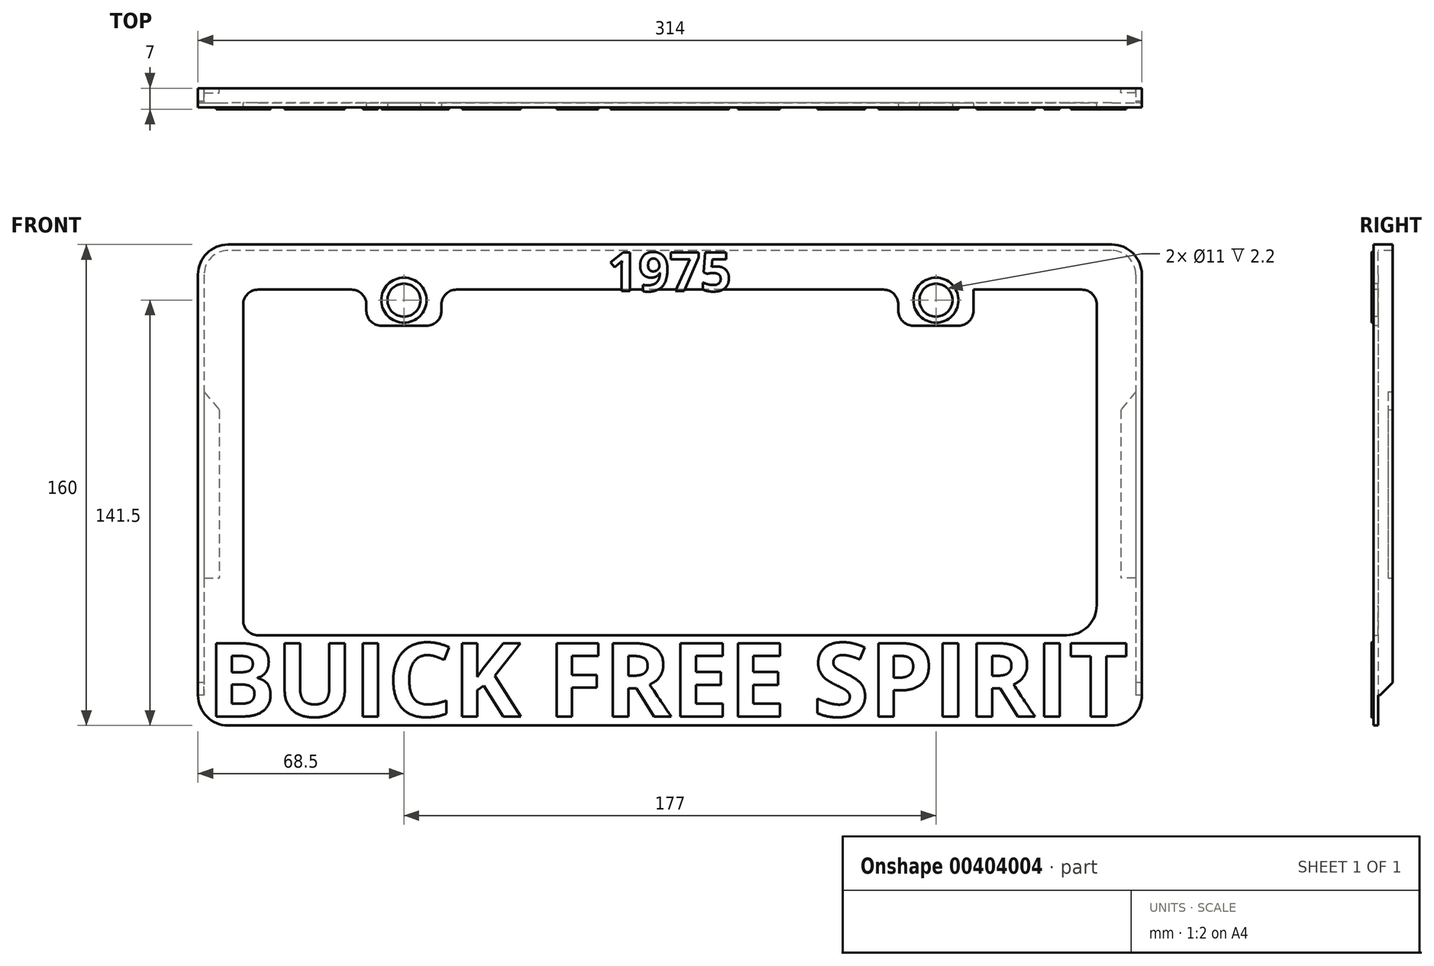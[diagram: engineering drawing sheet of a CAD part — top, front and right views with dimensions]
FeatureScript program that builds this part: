
annotation { "Feature Type Name" : "Feature", "Feature Type Description" : "" }
export const myFeature = defineFeature(function(context is Context, id is Id, definition is map)
    precondition{}
    {
        {
            var Q0;
            Q0=qCreatedBy(makeId("Front.planeOp"),FACE);
            var sketch = newSketch(context, id + "F0", { "sketchPlane" : qUnion([Q0])});
            skLineSegment(sketch, "E0.bottom", {"start": v(147, 80) * mm, "end": v(-147, 80) * mm});
            skLineSegment(sketch, "E0.top", {"start": v(147, -80) * mm, "end": v(-147, -80) * mm});
            skLineSegment(sketch, "E0.left", {"start": v(157, 70) * mm, "end": v(157, -70) * mm});
            skLineSegment(sketch, "E0.right", {"start": v(-157, 70) * mm, "end": v(-157, -70) * mm});
            skPoint(sketch, "E0.middle", {"position": v(0, 0) * mm});
            skLineSegment(sketch, "E1.bottom", {"start": v(137, 65) * mm, "end": v(-137, 65) * mm});
            skLineSegment(sketch, "E1.left", {"start": v(142, 60) * mm, "end": v(142, -40) * mm});
            skLineSegment(sketch, "E1.right", {"start": v(-142, 60) * mm, "end": v(-142, -45) * mm});
            skLineSegment(sketch, "E2", {"start": v(-137, -50) * mm, "end": v(132, -50) * mm});
            skPoint(sketch, "E3.orphan", {"position": v(142, -65) * mm});
            skPoint(sketch, "E4.orphan", {"position": v(-142, -65) * mm});
            skPoint(sketch, "E5.visualSharp", {"position": v(-157, 80) * mm});
            skArc(sketch, "E5.filletArc", {"start": v(-147, 80) * mm, "mid": v(-154.07, 77.07) * mm, "end": v(-157, 70) * mm});
            skPoint(sketch, "E6.visualSharp", {"position": v(-157, -80) * mm});
            skArc(sketch, "E6.filletArc", {"start": v(-157, -70) * mm, "mid": v(-154.07, -77.07) * mm, "end": v(-147, -80) * mm});
            skPoint(sketch, "E7.visualSharp", {"position": v(157, 80) * mm});
            skArc(sketch, "E7.filletArc", {"start": v(157, 70) * mm, "mid": v(154.07, 77.07) * mm, "end": v(147, 80) * mm});
            skPoint(sketch, "E8.visualSharp", {"position": v(157, -80) * mm});
            skArc(sketch, "E8.filletArc", {"start": v(147, -80) * mm, "mid": v(154.07, -77.07) * mm, "end": v(157, -70) * mm});
            skPoint(sketch, "E9.visualSharp", {"position": v(-142, 65) * mm});
            skArc(sketch, "E9.filletArc", {"start": v(-137, 65) * mm, "mid": v(-140.54, 63.54) * mm, "end": v(-142, 60) * mm});
            skPoint(sketch, "E10.visualSharp", {"position": v(-142, -50) * mm});
            skArc(sketch, "E10.filletArc", {"start": v(-142, -45) * mm, "mid": v(-140.54, -48.54) * mm, "end": v(-137, -50) * mm});
            skPoint(sketch, "E11.visualSharp", {"position": v(142, -50) * mm});
            skArc(sketch, "E11.filletArc", {"start": v(132, -50) * mm, "mid": v(139.07, -47.07) * mm, "end": v(142, -40) * mm});
            skPoint(sketch, "E12.visualSharp", {"position": v(142, 65) * mm});
            skArc(sketch, "E12.filletArc", {"start": v(142, 60) * mm, "mid": v(140.54, 63.54) * mm, "end": v(137, 65) * mm});
            skSolve(sketch);
        }
        {
            var Q0;
            Q0=qSketchRegion(id+"F0",true);
            extrude(context, id + "F1", {"entities" : qUnion([Q0]), "depth" : 1.6 * mm, "offsetDistance" : 25 * mm});
        }
        {
            var Q0;
            Q0=makeQuery(id+"F1.opExtrude","CAP_FACE",FACE,{"disambiguationData":[OSD([sQuery(id+"F0.wireOp",EDGE,"E0.bottom"),sQuery(id+"F0.wireOp",EDGE,"E0.top"),sQuery(id+"F0.wireOp",EDGE,"E0.left"),sQuery(id+"F0.wireOp",EDGE,"E0.right"),sQuery(id+"F0.wireOp",EDGE,"E1.bottom"),sQuery(id+"F0.wireOp",EDGE,"E1.left"),sQuery(id+"F0.wireOp",EDGE,"E1.right"),sQuery(id+"F0.wireOp",EDGE,"E2"),sQuery(id+"F0.wireOp",EDGE,"E5.filletArc"),sQuery(id+"F0.wireOp",EDGE,"E6.filletArc"),sQuery(id+"F0.wireOp",EDGE,"E7.filletArc"),sQuery(id+"F0.wireOp",EDGE,"E8.filletArc"),sQuery(id+"F0.wireOp",EDGE,"E9.filletArc"),sQuery(id+"F0.wireOp",EDGE,"E10.filletArc"),sQuery(id+"F0.wireOp",EDGE,"E11.filletArc"),sQuery(id+"F0.wireOp",EDGE,"E12.filletArc")])],"isStart":false});
            var sketch = newSketch(context, id + "F2", { "sketchPlane" : qUnion([Q0])});
            skLineSegment(sketch, "E13.bottom", {"start": v(-101, 65) * mm, "end": v(-76, 65) * mm});
            skLineSegment(sketch, "E13.top", {"start": v(-101, 53) * mm, "end": v(-76, 53) * mm});
            skLineSegment(sketch, "E13.left", {"start": v(-101, 65) * mm, "end": v(-101, 53) * mm});
            skLineSegment(sketch, "E13.right", {"start": v(-76, 65) * mm, "end": v(-76, 53) * mm});
            skLineSegment(sketch, "E14.bottom", {"start": v(76, 65) * mm, "end": v(101, 65) * mm});
            skLineSegment(sketch, "E14.top", {"start": v(76, 53) * mm, "end": v(101, 53) * mm});
            skLineSegment(sketch, "E14.left", {"start": v(76, 65) * mm, "end": v(76, 53) * mm});
            skLineSegment(sketch, "E14.right", {"start": v(101, 65) * mm, "end": v(101, 53) * mm});
            skLineSegment(sketch, "E15", {"start": v(-88.5, 53) * mm, "end": v(-88.5, 65) * mm, "construction": true});
            skLineSegment(sketch, "E16", {"start": v(-101, 53) * mm, "end": v(-142, 53) * mm, "construction": true});
            skLineSegment(sketch, "E17", {"start": v(101, 53) * mm, "end": v(142, 53) * mm, "construction": true});
            skSolve(sketch);
        }
        {
            var Q0;
            Q0=qSketchRegion(id+"F2",true);
            var Q1;
            Q1=makeQuery(id+"F1.opExtrude","CAP_FACE",FACE,{"disambiguationData":[OSD([sQuery(id+"F0.wireOp",EDGE,"E0.bottom"),sQuery(id+"F0.wireOp",EDGE,"E0.top"),sQuery(id+"F0.wireOp",EDGE,"E0.left"),sQuery(id+"F0.wireOp",EDGE,"E0.right"),sQuery(id+"F0.wireOp",EDGE,"E1.bottom"),sQuery(id+"F0.wireOp",EDGE,"E1.left"),sQuery(id+"F0.wireOp",EDGE,"E1.right"),sQuery(id+"F0.wireOp",EDGE,"E2"),sQuery(id+"F0.wireOp",EDGE,"E5.filletArc"),sQuery(id+"F0.wireOp",EDGE,"E6.filletArc"),sQuery(id+"F0.wireOp",EDGE,"E7.filletArc"),sQuery(id+"F0.wireOp",EDGE,"E8.filletArc"),sQuery(id+"F0.wireOp",EDGE,"E9.filletArc"),sQuery(id+"F0.wireOp",EDGE,"E10.filletArc"),sQuery(id+"F0.wireOp",EDGE,"E11.filletArc"),sQuery(id+"F0.wireOp",EDGE,"E12.filletArc")])],"isStart":true});
            extrude(context, id + "F3", {"entities" : qUnion([Q0]), "operationType" : NewBodyOperationType.ADD, "endBound" : BoundingType.UP_TO_SURFACE, "oppositeDirection" : true, "endBoundEntityFace" : qUnion([Q1]), "depth" : 25 * mm});
        }
        {
            var Q0;
            Q0=makeQuery(id+"F3.boolean.opBoolean","MERGE",FACE,{"derivedFrom":[makeQuery(id+"F1.opExtrude","CAP_FACE",FACE,{"disambiguationData":[OSD([sQuery(id+"F0.wireOp",EDGE,"E0.bottom"),sQuery(id+"F0.wireOp",EDGE,"E0.top"),sQuery(id+"F0.wireOp",EDGE,"E0.left"),sQuery(id+"F0.wireOp",EDGE,"E0.right"),sQuery(id+"F0.wireOp",EDGE,"E1.bottom"),sQuery(id+"F0.wireOp",EDGE,"E1.left"),sQuery(id+"F0.wireOp",EDGE,"E1.right"),sQuery(id+"F0.wireOp",EDGE,"E2"),sQuery(id+"F0.wireOp",EDGE,"E5.filletArc"),sQuery(id+"F0.wireOp",EDGE,"E6.filletArc"),sQuery(id+"F0.wireOp",EDGE,"E7.filletArc"),sQuery(id+"F0.wireOp",EDGE,"E8.filletArc"),sQuery(id+"F0.wireOp",EDGE,"E9.filletArc"),sQuery(id+"F0.wireOp",EDGE,"E10.filletArc"),sQuery(id+"F0.wireOp",EDGE,"E11.filletArc"),sQuery(id+"F0.wireOp",EDGE,"E12.filletArc")])],"isStart":false}),makeQuery(id+"F3.opExtrude","CAP_FACE",FACE,{"disambiguationData":[OSD([sQuery(id+"F2.wireOp",EDGE,"E13.bottom"),sQuery(id+"F2.wireOp",EDGE,"E13.top"),sQuery(id+"F2.wireOp",EDGE,"E13.left"),sQuery(id+"F2.wireOp",EDGE,"E13.right")])],"isStart":true}),makeQuery(id+"F3.opExtrude","CAP_FACE",FACE,{"disambiguationData":[OSD([sQuery(id+"F2.wireOp",EDGE,"E14.bottom"),sQuery(id+"F2.wireOp",EDGE,"E14.top"),sQuery(id+"F2.wireOp",EDGE,"E14.left"),sQuery(id+"F2.wireOp",EDGE,"E14.right")])],"isStart":true})]});
            var sketch = newSketch(context, id + "F4", { "sketchPlane" : qUnion([Q0])});
            skLineSegment(sketch, "E18", {"start": v(101, 55) * mm, "end": v(101, 65) * mm});
            skLineSegment(sketch, "E19", {"start": v(101, 55) * mm, "end": v(142, 55) * mm});
            skLineSegment(sketch, "E20", {"start": v(142, 60) * mm, "end": v(101, 60) * mm});
            skLineSegment(sketch, "E21", {"start": v(142, 55) * mm, "end": v(142, 60) * mm});
            skLineSegment(sketch, "E22", {"start": v(101, 65) * mm, "end": v(101, 60) * mm});
            skSolve(sketch);
        }
        {
            var Q0;
            Q0=makeQuery(id+"F3.opExtrude","SWEPT_EDGE",EDGE,{"disambiguationData":[OSD([sQuery(id+"F2.wireOp",EDGE,"E13.top"),sQuery(id+"F2.wireOp",EDGE,"E13.left")])]});
            var Q1;
            Q1=makeQuery(id+"F3.opExtrude","SWEPT_EDGE",EDGE,{"disambiguationData":[OSD([sQuery(id+"F0.wireOp",EDGE,"E1.bottom"),sQuery(id+"F2.wireOp",EDGE,"E13.bottom"),sQuery(id+"F2.wireOp",EDGE,"E13.left")])]});
            var Q2;
            Q2=makeQuery(id+"F3.opExtrude","SWEPT_EDGE",EDGE,{"disambiguationData":[OSD([sQuery(id+"F2.wireOp",EDGE,"E13.top"),sQuery(id+"F2.wireOp",EDGE,"E13.right")])]});
            var Q3;
            Q3=makeQuery(id+"F3.opExtrude","SWEPT_EDGE",EDGE,{"disambiguationData":[OSD([sQuery(id+"F0.wireOp",EDGE,"E1.bottom"),sQuery(id+"F2.wireOp",EDGE,"E13.bottom"),sQuery(id+"F2.wireOp",EDGE,"E13.right")])]});
            var Q4;
            Q4=makeQuery(id+"F3.opExtrude","SWEPT_EDGE",EDGE,{"disambiguationData":[OSD([sQuery(id+"F2.wireOp",EDGE,"E14.top"),sQuery(id+"F2.wireOp",EDGE,"E14.right")])]});
            var Q5;
            Q5=makeQuery(id+"F3.opExtrude","SWEPT_EDGE",EDGE,{"disambiguationData":[OSD([sQuery(id+"F0.wireOp",EDGE,"E1.bottom"),sQuery(id+"F2.wireOp",EDGE,"E14.bottom"),sQuery(id+"F2.wireOp",EDGE,"E14.right")])]});
            var Q6;
            Q6=makeQuery(id+"F3.opExtrude","SWEPT_EDGE",EDGE,{"disambiguationData":[OSD([sQuery(id+"F2.wireOp",EDGE,"E14.top"),sQuery(id+"F2.wireOp",EDGE,"E14.left")])]});
            var Q7;
            Q7=makeQuery(id+"F3.opExtrude","SWEPT_EDGE",EDGE,{"disambiguationData":[OSD([sQuery(id+"F0.wireOp",EDGE,"E1.bottom"),sQuery(id+"F2.wireOp",EDGE,"E14.bottom"),sQuery(id+"F2.wireOp",EDGE,"E14.left")])]});
            var Q8;
            Q8=makeQuery(id+"FJHd9evdb0oNIyS_1.boolean.opBoolean","COPY",EDGE,{"derivedFrom":makeQuery(id+"FJHd9evdb0oNIyS_1.opExtrude","SWEPT_EDGE",EDGE,{"disambiguationData":[OSD([sQuery(id+"F4.wireOp",EDGE,"E19"),sQuery(id+"F4.wireOp",EDGE,"E21")])]})});
            fillet(context, id + "F5", {"entities" : qUnion([Q0, Q1, Q2, Q3, Q4, Q5, Q6, Q7, Q8]), "radius" : 5 * mm, "tangentPropagation" : true, "allowEdgeOverflow" : false});
        }
        {
            var Q0;
            Q0=makeQuery(id+"F3.boolean.opBoolean","MERGE",FACE,{"derivedFrom":[makeQuery(id+"F1.opExtrude","CAP_FACE",FACE,{"disambiguationData":[OSD([sQuery(id+"F0.wireOp",EDGE,"E0.bottom"),sQuery(id+"F0.wireOp",EDGE,"E0.top"),sQuery(id+"F0.wireOp",EDGE,"E0.left"),sQuery(id+"F0.wireOp",EDGE,"E0.right"),sQuery(id+"F0.wireOp",EDGE,"E1.bottom"),sQuery(id+"F0.wireOp",EDGE,"E1.left"),sQuery(id+"F0.wireOp",EDGE,"E1.right"),sQuery(id+"F0.wireOp",EDGE,"E2"),sQuery(id+"F0.wireOp",EDGE,"E5.filletArc"),sQuery(id+"F0.wireOp",EDGE,"E6.filletArc"),sQuery(id+"F0.wireOp",EDGE,"E7.filletArc"),sQuery(id+"F0.wireOp",EDGE,"E8.filletArc"),sQuery(id+"F0.wireOp",EDGE,"E9.filletArc"),sQuery(id+"F0.wireOp",EDGE,"E10.filletArc"),sQuery(id+"F0.wireOp",EDGE,"E11.filletArc"),sQuery(id+"F0.wireOp",EDGE,"E12.filletArc")])],"isStart":false}),makeQuery(id+"F3.opExtrude","CAP_FACE",FACE,{"disambiguationData":[OSD([sQuery(id+"F2.wireOp",EDGE,"E13.bottom"),sQuery(id+"F2.wireOp",EDGE,"E13.top"),sQuery(id+"F2.wireOp",EDGE,"E13.left"),sQuery(id+"F2.wireOp",EDGE,"E13.right")])],"isStart":true}),makeQuery(id+"F3.opExtrude","CAP_FACE",FACE,{"disambiguationData":[OSD([sQuery(id+"F2.wireOp",EDGE,"E14.bottom"),sQuery(id+"F2.wireOp",EDGE,"E14.top"),sQuery(id+"F2.wireOp",EDGE,"E14.left"),sQuery(id+"F2.wireOp",EDGE,"E14.right")])],"isStart":true})]});
            var sketch = newSketch(context, id + "F6", { "sketchPlane" : qUnion([Q0])});
            skCircle(sketch, "E23", {"center": v(-88.5, 61.5) * mm, "radius": 5.5 * mm});
            skCircle(sketch, "E24", {"center": v(88.5, 61.5) * mm, "radius": 5.5 * mm});
            skLineSegment(sketch, "E25", {"start": v(-88.5, 49) * mm, "end": v(-88.5, 94.48) * mm, "construction": true});
            skLineSegment(sketch, "E26", {"start": v(88.5, 49) * mm, "end": v(88.5, 72.42) * mm, "construction": true});
            skSolve(sketch);
        }
        {
            var Q0;
            Q0=qSketchRegion(id+"F6",true);
            extrude(context, id + "F7", {"entities" : qUnion([Q0]), "operationType" : NewBodyOperationType.REMOVE, "oppositeDirection" : true, "depth" : 25 * mm});
        }
        {
            var Q0;
            Q0=makeQuery(id+"F3.boolean.opBoolean","MERGE",FACE,{"derivedFrom":[makeQuery(id+"F1.opExtrude","CAP_FACE",FACE,{"disambiguationData":[OSD([sQuery(id+"F0.wireOp",EDGE,"E0.bottom"),sQuery(id+"F0.wireOp",EDGE,"E0.top"),sQuery(id+"F0.wireOp",EDGE,"E0.left"),sQuery(id+"F0.wireOp",EDGE,"E0.right"),sQuery(id+"F0.wireOp",EDGE,"E1.bottom"),sQuery(id+"F0.wireOp",EDGE,"E1.left"),sQuery(id+"F0.wireOp",EDGE,"E1.right"),sQuery(id+"F0.wireOp",EDGE,"E2"),sQuery(id+"F0.wireOp",EDGE,"E5.filletArc"),sQuery(id+"F0.wireOp",EDGE,"E6.filletArc"),sQuery(id+"F0.wireOp",EDGE,"E7.filletArc"),sQuery(id+"F0.wireOp",EDGE,"E8.filletArc"),sQuery(id+"F0.wireOp",EDGE,"E9.filletArc"),sQuery(id+"F0.wireOp",EDGE,"E10.filletArc"),sQuery(id+"F0.wireOp",EDGE,"E11.filletArc"),sQuery(id+"F0.wireOp",EDGE,"E12.filletArc")])],"isStart":false}),makeQuery(id+"F3.opExtrude","CAP_FACE",FACE,{"disambiguationData":[OSD([sQuery(id+"F2.wireOp",EDGE,"E13.bottom"),sQuery(id+"F2.wireOp",EDGE,"E13.top"),sQuery(id+"F2.wireOp",EDGE,"E13.left"),sQuery(id+"F2.wireOp",EDGE,"E13.right")])],"isStart":true}),makeQuery(id+"F3.opExtrude","CAP_FACE",FACE,{"disambiguationData":[OSD([sQuery(id+"F2.wireOp",EDGE,"E14.bottom"),sQuery(id+"F2.wireOp",EDGE,"E14.top"),sQuery(id+"F2.wireOp",EDGE,"E14.left"),sQuery(id+"F2.wireOp",EDGE,"E14.right")])],"isStart":true})]});
            var sketch = newSketch(context, id + "F8", { "sketchPlane" : qUnion([Q0])});
            skText(sketch, "E27", { "text": "1975", "fontName": "OpenSans-Bold.ttf"});
            const initialGuessF8  = {"E27": [-0.0208, 0.0645, 1, 0, 0.013]};
            skSetInitialGuess(sketch, initialGuessF8);
            skSolve(sketch);
        }
        {
            var Q0;
            Q0=qSketchRegion(id+"F8",true);
            extrude(context, id + "F9", {"entities" : qUnion([Q0]), "operationType" : NewBodyOperationType.ADD, "offsetDistance" : 25 * mm, "depth" : .6 * mm});
        }
        {
            var Q0;
            {var subQ0=sQuery(id+"F0.wireOp",EDGE,"E0.right");var subQ2=sQuery(id+"F2.wireOp",EDGE,"E14.left");var subQ3=sQuery(id+"F2.wireOp",EDGE,"E14.bottom");var subQ4=sQuery(id+"F0.wireOp",EDGE,"E1.bottom");var subQ5=sQuery(id+"F2.wireOp",EDGE,"E14.right");var subQ6=sQuery(id+"F2.wireOp",EDGE,"E14.top");var subQ7=sQuery(id+"F0.wireOp",EDGE,"E8.filletArc");var subQ8=sQuery(id+"F0.wireOp",EDGE,"E5.filletArc");var subQ9=sQuery(id+"F0.wireOp",EDGE,"E7.filletArc");var subQ10=sQuery(id+"F0.wireOp",EDGE,"E2");var subQ11=sQuery(id+"F0.wireOp",EDGE,"E6.filletArc");var subQ12=sQuery(id+"F0.wireOp",EDGE,"E1.right");var subQ13=sQuery(id+"F2.wireOp",EDGE,"E13.right");var subQ14=sQuery(id+"F2.wireOp",EDGE,"E13.top");var subQ15=sQuery(id+"F0.wireOp",EDGE,"E1.left");var subQ16=sQuery(id+"F0.wireOp",EDGE,"E9.filletArc");var subQ17=sQuery(id+"F2.wireOp",EDGE,"E13.bottom");var subQ18=sQuery(id+"F0.wireOp",EDGE,"E0.bottom");var subQ19=sQuery(id+"F0.wireOp",EDGE,"E0.top");var subQ20=sQuery(id+"F0.wireOp",EDGE,"E0.left");var subQ21=sQuery(id+"F0.wireOp",EDGE,"E10.filletArc");var subQ23=sQuery(id+"F2.wireOp",EDGE,"E13.left");var subQ24=sQuery(id+"F0.wireOp",EDGE,"E11.filletArc");Q0=makeQuery(id+"F9.boolean.opBoolean","SPLIT",FACE,{"disambiguationData":[TD([makeQuery(id+"F1.opExtrude","SWEPT_FACE",FACE,{"disambiguationData":[OSD([subQ18])]})])],"derivedFrom":makeQuery(id+"F3.boolean.opBoolean","MERGE",FACE,{"derivedFrom":[makeQuery(id+"F1.opExtrude","CAP_FACE",FACE,{"disambiguationData":[OSD([subQ18,subQ19,subQ20,subQ0,subQ4,subQ15,subQ12,subQ10,subQ8,subQ11,subQ9,subQ7,subQ16,subQ21,subQ24,sQuery(id+"F0.wireOp",EDGE,"E12.filletArc")])],"isStart":false}),makeQuery(id+"F3.opExtrude","CAP_FACE",FACE,{"disambiguationData":[OSD([subQ17,subQ14,subQ23,subQ13])],"isStart":true}),makeQuery(id+"F3.opExtrude","CAP_FACE",FACE,{"disambiguationData":[OSD([subQ3,subQ6,subQ2,subQ5])],"isStart":true})]})});}
            var sketch = newSketch(context, id + "F10", { "sketchPlane" : qUnion([Q0])});
            skText(sketch, "E28", { "text": "75", "fontName": "OpenSans-Bold.ttf"});
            const initialGuessF10  = {"E28": [0.11823, -0.0765, 1, 0, 0.02]};
            skSetInitialGuess(sketch, initialGuessF10);
            skSolve(sketch);
        }
        {
            var Q0;
            {var subQ0=sQuery(id+"F0.wireOp",EDGE,"E0.right");var subQ2=sQuery(id+"F2.wireOp",EDGE,"E14.left");var subQ3=sQuery(id+"F2.wireOp",EDGE,"E14.bottom");var subQ4=sQuery(id+"F0.wireOp",EDGE,"E1.bottom");var subQ5=sQuery(id+"F2.wireOp",EDGE,"E14.right");var subQ6=sQuery(id+"F2.wireOp",EDGE,"E14.top");var subQ7=sQuery(id+"F0.wireOp",EDGE,"E8.filletArc");var subQ8=sQuery(id+"F0.wireOp",EDGE,"E5.filletArc");var subQ9=sQuery(id+"F0.wireOp",EDGE,"E7.filletArc");var subQ10=sQuery(id+"F0.wireOp",EDGE,"E2");var subQ11=sQuery(id+"F0.wireOp",EDGE,"E6.filletArc");var subQ12=sQuery(id+"F0.wireOp",EDGE,"E1.right");var subQ13=sQuery(id+"F2.wireOp",EDGE,"E13.right");var subQ14=sQuery(id+"F2.wireOp",EDGE,"E13.top");var subQ15=sQuery(id+"F0.wireOp",EDGE,"E1.left");var subQ16=sQuery(id+"F0.wireOp",EDGE,"E9.filletArc");var subQ17=sQuery(id+"F2.wireOp",EDGE,"E13.bottom");var subQ18=sQuery(id+"F0.wireOp",EDGE,"E0.bottom");var subQ19=sQuery(id+"F0.wireOp",EDGE,"E0.top");var subQ20=sQuery(id+"F0.wireOp",EDGE,"E0.left");var subQ21=sQuery(id+"F0.wireOp",EDGE,"E10.filletArc");var subQ23=sQuery(id+"F2.wireOp",EDGE,"E13.left");var subQ24=sQuery(id+"F0.wireOp",EDGE,"E11.filletArc");Q0=makeQuery(id+"F9.boolean.opBoolean","SPLIT",FACE,{"disambiguationData":[TD([makeQuery(id+"F1.opExtrude","SWEPT_FACE",FACE,{"disambiguationData":[OSD([subQ18])]})])],"derivedFrom":makeQuery(id+"F3.boolean.opBoolean","MERGE",FACE,{"derivedFrom":[makeQuery(id+"F1.opExtrude","CAP_FACE",FACE,{"disambiguationData":[OSD([subQ18,subQ19,subQ20,subQ0,subQ4,subQ15,subQ12,subQ10,subQ8,subQ11,subQ9,subQ7,subQ16,subQ21,subQ24,sQuery(id+"F0.wireOp",EDGE,"E12.filletArc")])],"isStart":false}),makeQuery(id+"F3.opExtrude","CAP_FACE",FACE,{"disambiguationData":[OSD([subQ17,subQ14,subQ23,subQ13])],"isStart":true}),makeQuery(id+"F3.opExtrude","CAP_FACE",FACE,{"disambiguationData":[OSD([subQ3,subQ6,subQ2,subQ5])],"isStart":true})]})});}
            var sketch = newSketch(context, id + "F11", { "sketchPlane" : qUnion([Q0])});
            skText(sketch, "E29", { "text": "BUICK FREE SPIRIT", "fontName": "OpenSans-Bold.ttf"});
            const initialGuessF11  = {"E29": [-0.154, -0.077, 1, 0, 0.02455]};
            skSetInitialGuess(sketch, initialGuessF11);
            skSolve(sketch);
        }
        {
            var Q0;
            Q0=qSketchRegion(id+"F11",true);
            extrude(context, id + "F12", {"entities" : qUnion([Q0]), "operationType" : NewBodyOperationType.ADD, "offsetDistance" : 25 * mm, "depth" : .6 * mm});
        }
        {
            var Q0;
            {var subQ0=sQuery(id+"F0.wireOp",EDGE,"E12.filletArc");var subQ1=sQuery(id+"F0.wireOp",EDGE,"E11.filletArc");var subQ2=sQuery(id+"F0.wireOp",EDGE,"E10.filletArc");var subQ3=sQuery(id+"F0.wireOp",EDGE,"E9.filletArc");var subQ4=sQuery(id+"F0.wireOp",EDGE,"E8.filletArc");var subQ5=sQuery(id+"F0.wireOp",EDGE,"E7.filletArc");var subQ6=sQuery(id+"F0.wireOp",EDGE,"E6.filletArc");var subQ7=sQuery(id+"F0.wireOp",EDGE,"E5.filletArc");var subQ8=sQuery(id+"F0.wireOp",EDGE,"E2");var subQ9=sQuery(id+"F0.wireOp",EDGE,"E1.right");var subQ10=sQuery(id+"F0.wireOp",EDGE,"E1.left");var subQ11=sQuery(id+"F0.wireOp",EDGE,"E1.bottom");var subQ12=sQuery(id+"F0.wireOp",EDGE,"E0.right");var subQ13=sQuery(id+"F0.wireOp",EDGE,"E0.left");var subQ14=sQuery(id+"F0.wireOp",EDGE,"E0.top");var subQ15=sQuery(id+"F0.wireOp",EDGE,"E0.bottom");Q0=makeQuery(id+"F3.boolean.opBoolean","MERGE",FACE,{"derivedFrom":[makeQuery(id+"F1.opExtrude","CAP_FACE",FACE,{"disambiguationData":[OSD([subQ15,subQ14,subQ13,subQ12,subQ11,subQ10,subQ9,subQ8,subQ7,subQ6,subQ5,subQ4,subQ3,subQ2,subQ1,subQ0])],"isStart":true}),makeQuery(id+"F3.opExtrude","CAP_FACE",FACE,{"disambiguationData":[OSD([subQ15,subQ14,subQ13,subQ12,subQ11,subQ10,subQ9,subQ8,subQ7,subQ6,subQ5,subQ4,subQ3,subQ2,subQ1,subQ0]),ownerDisambiguation([makeQuery(id+"F2.imprint","IMPRINT",EDGE,{"derivedFrom":sQuery(id+"F2.wireOp",EDGE,"E13.bottom")})])],"isStart":false}),makeQuery(id+"F3.opExtrude","CAP_FACE",FACE,{"disambiguationData":[OSD([subQ15,subQ14,subQ13,subQ12,subQ11,subQ10,subQ9,subQ8,subQ7,subQ6,subQ5,subQ4,subQ3,subQ2,subQ1,subQ0]),ownerDisambiguation([makeQuery(id+"F2.imprint","IMPRINT",EDGE,{"derivedFrom":sQuery(id+"F2.wireOp",EDGE,"E14.bottom")})])],"isStart":false})]});}
            var sketch = newSketch(context, id + "F13", { "sketchPlane" : qUnion([Q0])});
            skLineSegment(sketch, "E30.0", {"start": v(-157, 70) * mm, "end": v(-157, -70) * mm});
            skLineSegment(sketch, "E31.0", {"start": v(-147, 80) * mm, "end": v(147, 80) * mm});
            skLineSegment(sketch, "E32.0", {"start": v(157, 70) * mm, "end": v(157, -70) * mm});
            skArc(sketch, "E33.0", {"start": v(147, 80) * mm, "mid": v(154.07, 77.07) * mm, "end": v(157, 70) * mm});
            skLineSegment(sketch, "E34.0", {"start": v(-155, 70) * mm, "end": v(-155, -70) * mm});
            skLineSegment(sketch, "E34.1", {"start": v(155, 70) * mm, "end": v(155, -70) * mm});
            skArc(sketch, "E34.2", {"start": v(147, 78) * mm, "mid": v(152.66, 75.66) * mm, "end": v(155, 70) * mm});
            skLineSegment(sketch, "E34.3", {"start": v(-147, 78) * mm, "end": v(147, 78) * mm});
            skArc(sketch, "E34.4", {"start": v(-155, 70) * mm, "mid": v(-152.66, 75.66) * mm, "end": v(-147, 78) * mm});
            skLineSegment(sketch, "E35", {"start": v(-157, -70) * mm, "end": v(-155, -70) * mm});
            skLineSegment(sketch, "E36", {"start": v(155, -70) * mm, "end": v(157, -70) * mm});
            skSolve(sketch);
        }
        {
            var Q0;
            Q0=makeQuery(id+"F13.imprint","IMPRINT",FACE,{"disambiguationData":[TD([[makeQuery(id+"F13.imprint","IMPRINT",EDGE,{"derivedFrom":sQuery(id+"F13.wireOp",EDGE,"E30.0")}),1.0]])]});
            extrude(context, id + "F14", {"entities" : qUnion([Q0]), "operationType" : NewBodyOperationType.ADD, "offsetDistance" : 25 * mm, "depth" : 4.8 * mm});
        }
        {
            var Q0;
            Q0=makeQuery(id+"F14.opExtrude","CAP_FACE",FACE,{"disambiguationData":[OSD([sQuery(id+"F0.wireOp",EDGE,"E7.filletArc"),sQuery(id+"F13.wireOp",EDGE,"E30.0"),sQuery(id+"F13.wireOp",EDGE,"E31.0"),sQuery(id+"F13.wireOp",EDGE,"E32.0"),sQuery(id+"F13.wireOp",EDGE,"E33.0"),sQuery(id+"F13.wireOp",EDGE,"E34.0"),sQuery(id+"F13.wireOp",EDGE,"E34.1"),sQuery(id+"F13.wireOp",EDGE,"E34.2"),sQuery(id+"F13.wireOp",EDGE,"E34.3"),sQuery(id+"F13.wireOp",EDGE,"E34.4"),sQuery(id+"F13.wireOp",EDGE,"E35"),sQuery(id+"F13.wireOp",EDGE,"E36")])],"isStart":false});
            var sketch = newSketch(context, id + "F15", { "sketchPlane" : qUnion([Q0])});
            skLineSegment(sketch, "E37.top", {"start": v(-155, -31) * mm, "end": v(-150, -31) * mm});
            skLineSegment(sketch, "E37.left", {"start": v(-155, 31) * mm, "end": v(-155, -31) * mm});
            skLineSegment(sketch, "E37.right", {"start": v(-150, 25.04) * mm, "end": v(-150, -31) * mm});
            skLineSegment(sketch, "E38", {"start": v(-150, 0) * mm, "end": v(-99.43, 0) * mm, "construction": true});
            skLineSegment(sketch, "E39", {"start": v(0, 0) * mm, "end": v(0, 29.16) * mm, "construction": true});
            skLineSegment(sketch, "E40.MirrorCS", {"start": v(155, -31) * mm, "end": v(150, -31) * mm});
            skLineSegment(sketch, "E41.MirrorCS", {"start": v(155, 31) * mm, "end": v(155, -31) * mm});
            skLineSegment(sketch, "E42.MirrorCS", {"start": v(150, 25.04) * mm, "end": v(150, -31) * mm});
            skLineSegment(sketch, "E43", {"start": v(155, 31) * mm, "end": v(150, 25.04) * mm});
            skPoint(sketch, "E44.MirrorCS.end.orphan", {"position": v(150, 31) * mm});
            skPoint(sketch, "E44.MirrorCS.start.orphan", {"position": v(155, 31) * mm});
            skLineSegment(sketch, "E45", {"start": v(-155, 31) * mm, "end": v(-150, 25.04) * mm});
            skPoint(sketch, "E37.bottom.end.orphan", {"position": v(-150, 31) * mm});
            skSolve(sketch);
        }
        {
            var Q0;
            Q0=qSketchRegion(id+"F15",true);
            extrude(context, id + "F16", {"entities" : qUnion([Q0]), "operationType" : NewBodyOperationType.ADD, "oppositeDirection" : true, "depth" : 1.6 * mm});
        }
        {
            var Q0;
            Q0=makeQuery(id+"F14.opExtrude","CAP_EDGE",EDGE,{"disambiguationData":[OSD([sQuery(id+"F13.wireOp",EDGE,"E36")])],"isStart":false});
            var Q1;
            Q1=makeQuery(id+"F14.opExtrude","CAP_EDGE",EDGE,{"disambiguationData":[OSD([sQuery(id+"F13.wireOp",EDGE,"E35")])],"isStart":false});
            chamfer(context, id + "F17", {"entities" : qUnion([Q0, Q1]), "width" : 4.2 * mm, "tangentPropagation" : true});
        }
        {
            var Q0;
            {var subQ16=sQuery(id+"F4.wireOp",EDGE,"E18");Q0=makeQuery(id+"F4.imprint","IMPRINT",FACE,{"disambiguationData":[TD([[makeQuery(id+"F4.imprint","IMPRINT",EDGE,{"derivedFrom":subQ16}),-1.0]])]});}
            var sketch = newSketch(context, id + "F18", { "sketchPlane" : qUnion([Q0])});
            skCircle(sketch, "E46", {"center": v(-88.5, 61.5) * mm, "radius": 7.5 * mm});
            skCircle(sketch, "E47.0", {"center": v(-88.5, 61.5) * mm, "radius": 5.5 * mm});
            skCircle(sketch, "E48", {"center": v(88.5, 61.5) * mm, "radius": 7.5 * mm});
            skCircle(sketch, "E49.0", {"center": v(88.5, 61.5) * mm, "radius": 5.5 * mm});
            skSolve(sketch);
        }
        {
            var Q0;
            Q0 = qSketchRegion(id + "F18", true);
            extrude(context, id + "F19", {"entities" : qUnion([Q0]), "operationType" : NewBodyOperationType.ADD, "depth" : .6 * mm, "offsetDistance" : 25 * mm});
        }
    });
